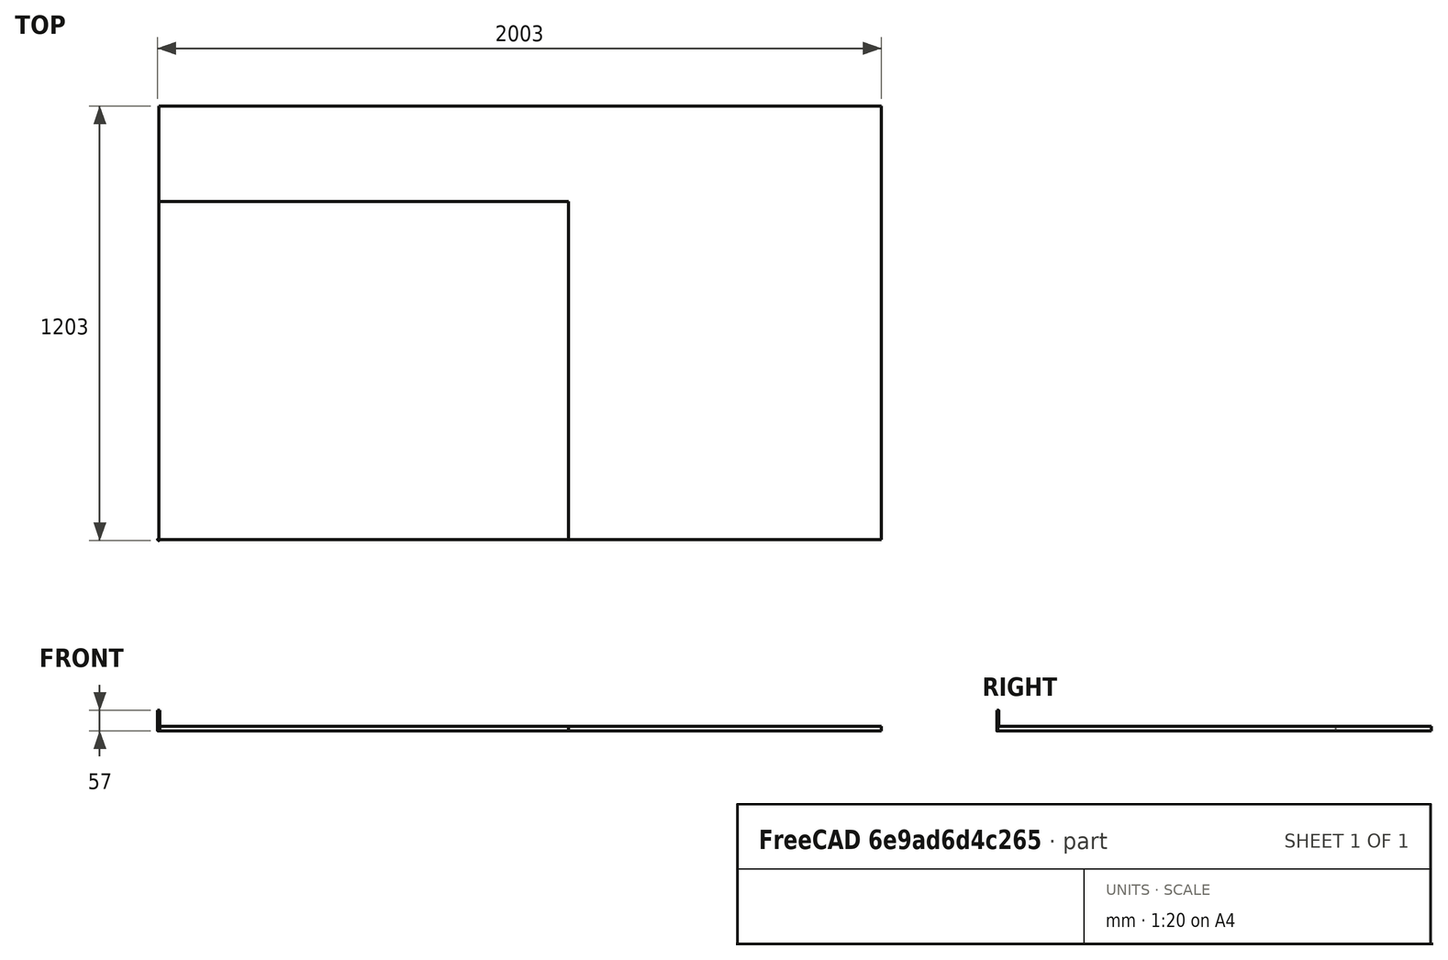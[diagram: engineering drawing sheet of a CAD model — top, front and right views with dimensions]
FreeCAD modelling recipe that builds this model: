
FCSTD DOCUMENT  (FreeCAD 0.21R33771 (Git))
Label: Doll House
License: All rights reserved
LicenseURL: http://en.wikipedia.org/wiki/All_rights_reserved
objects: Part::FeaturePython×10, Sketcher::SketchObject×9, PartDesign::Pad×6, PartDesign::Body×6, Path::FeaturePython×5, PartDesign::Pocket×3, Part::Mirroring×3, App::DocumentObjectGroup×3, App::FeaturePython×1, Mesh::FeaturePython×1
note: 49 computed .brp shape members not serialized (recipe doc carries the construction recipe); baked Part::Feature solids carry a one-line shape summary decoded from their .brp

FEATURE [Sketcher::SketchObject] Sketch
  FullyConstrained = true
  MapMode = 5
  Support = -> [XY_Plane]
  sketch-geometry (4):
    g0: LineSegment StartX=0 StartY=0 StartZ=0 EndX=2000 EndY=0 EndZ=0
    g1: LineSegment StartX=2000 StartY=0 StartZ=0 EndX=2000 EndY=1200 EndZ=0
    g2: LineSegment StartX=2000 StartY=1200 StartZ=0 EndX=0 EndY=1200 EndZ=0
    g3: LineSegment StartX=0 StartY=1200 StartZ=0 EndX=0 EndY=0 EndZ=0
  constraints (11):
    c: Coincident(g0,g1)
    c: Coincident(g1,g2)
    c: Coincident(g2,g3)
    c: Coincident(g3,g0)
    c: Horizontal(g0)
    c: Horizontal(g2)
    c: Vertical(g1)
    c: Vertical(g3)
    c: Coincident(g0,g-1)
    c: DistanceY(g3,g3) = 1200
    c: DistanceX(g0,g0) = 2000
FEATURE [PartDesign::Pad] Pad
  Direction = (0,0,1)
  Length = 12.7
  Length2 = 10
  Profile = -> Sketch
  ReferenceAxis = -> Sketch [N_Axis]
  Type = 0
FEATURE [PartDesign::Body] Body
  Group = -> [Sketch,Pad]
  Origin = -> Origin
  Tip = -> Pad
FEATURE [Sketcher::SketchObject] Sketch001
  FullyConstrained = true
  MapMode = 5
  Support = -> [XY_Plane001]
  sketch-geometry (5):
    g0: LineSegment StartX=0 StartY=0 StartZ=0 EndX=600 EndY=0 EndZ=0
    g1: LineSegment StartX=600 StartY=0 StartZ=0 EndX=600 EndY=350 EndZ=0
    g2: LineSegment StartX=0 StartY=350 StartZ=0 EndX=0 EndY=0 EndZ=0
    g3: LineSegment StartX=0 StartY=350 StartZ=0 EndX=300 EndY=400 EndZ=0
    g4: LineSegment StartX=300 StartY=400 StartZ=0 EndX=600 EndY=350 EndZ=0
  constraints (14):
    c: Coincident(g0,g1)
    c: Coincident(g2,g0)
    c: Horizontal(g0)
    c: Vertical(g1)
    c: Vertical(g2)
    c: Coincident(g0,g-1)
    c: DistanceX(g2,g1) = 600
    c: DistanceY(g1,g1) = 350
    c: Coincident(g3,g4)
    c: Coincident(g4,g1)
    c: Equal(g3,g4)
    c: DistanceY(g0,g3) = 400
    c: Coincident(g2,g3)
    c: DistanceY(g2,g2) = 350
FEATURE [PartDesign::Pad] Pad001
  Direction = (0,0,1)
  Length = 12.7
  Length2 = 10
  Profile = -> Sketch001
  ReferenceAxis = -> Sketch001 [N_Axis]
  Type = 0
FEATURE [PartDesign::Body] Body001  label="Rear"
  Group = -> [Sketch001,Pad001]
  Origin = -> Origin001
  Tip = -> Pad001
FEATURE [Sketcher::SketchObject] Sketch002
  FullyConstrained = false
  MapMode = 5
  Support = -> [XY_Plane002]
  expr: Constraints[10] = 600
  sketch-geometry (4):
    g0: LineSegment StartX=0 StartY=666.245 StartZ=0 EndX=600 EndY=666.245 EndZ=0
    g1: LineSegment StartX=600 StartY=666.245 StartZ=0 EndX=600 EndY=416.245 EndZ=0
    g2: LineSegment StartX=600 StartY=416.245 StartZ=0 EndX=0 EndY=416.245 EndZ=0
    g3: LineSegment StartX=0 StartY=416.245 StartZ=0 EndX=0 EndY=666.245 EndZ=0
  constraints (11):
    c: Coincident(g0,g1)
    c: Coincident(g1,g2)
    c: Coincident(g2,g3)
    c: Coincident(g3,g0)
    c: Horizontal(g0)
    c: Horizontal(g2)
    c: Vertical(g1)
    c: Vertical(g3)
    c: DistanceY(g3,g3) = 250
    c: PointOnObject(g2,g-2)
    c: DistanceX(g0,g0) = 600
FEATURE [PartDesign::Pad] Pad002
  Direction = (0,0,1)
  Length = 12.7
  Length2 = 10
  Profile = -> Sketch002
  ReferenceAxis = -> Sketch002 [N_Axis]
  Type = 0
FEATURE [Sketcher::SketchObject] Sketch004
  FullyConstrained = false
  MapMode = 5
  Support = -> [XY_Plane004]
  sketch-geometry (16):
    g0: LineSegment StartX=624.003 StartY=0 StartZ=0 EndX=874.003 EndY=0 EndZ=0
    g1: LineSegment StartX=874.003 StartY=0 StartZ=0 EndX=874.003 EndY=350 EndZ=0
    g2: LineSegment StartX=874.003 StartY=350 StartZ=0 EndX=624.003 EndY=350 EndZ=0
    g3: LineSegment StartX=624.003 StartY=350 StartZ=0 EndX=624.003 EndY=0 EndZ=0
    g4: LineSegment StartX=659.003 StartY=325 StartZ=0 EndX=731.518 EndY=325 EndZ=0
    g5: LineSegment StartX=731.518 StartY=325 StartZ=0 EndX=731.518 EndY=245.545 EndZ=0
    g6: LineSegment StartX=731.518 StartY=245.545 StartZ=0 EndX=659.003 EndY=245.545 EndZ=0
    g7: LineSegment StartX=659.003 StartY=245.545 StartZ=0 EndX=659.003 EndY=325 EndZ=0
    g8: LineSegment StartX=766.489 StartY=325 StartZ=0 EndX=839.003 EndY=325 EndZ=0
    g9: LineSegment StartX=839.003 StartY=325 StartZ=0 EndX=839.003 EndY=245.545 EndZ=0
    g10: LineSegment StartX=839.003 StartY=245.545 StartZ=0 EndX=766.489 EndY=245.545 EndZ=0
    g11: LineSegment StartX=766.489 StartY=245.545 StartZ=0 EndX=766.489 EndY=325 EndZ=0
    g12: LineSegment StartX=702.358 StartY=126.524 StartZ=0 EndX=796.107 EndY=126.524 EndZ=0
    g13: LineSegment StartX=796.107 StartY=126.524 StartZ=0 EndX=796.107 EndY=45.8183 EndZ=0
    g14: LineSegment StartX=796.107 StartY=45.8183 StartZ=0 EndX=702.358 EndY=45.8183 EndZ=0
    g15: LineSegment StartX=702.358 StartY=45.8183 StartZ=0 EndX=702.358 EndY=126.524 EndZ=0
  constraints (41):
    c: Coincident(g0,g1)
    c: Coincident(g1,g2)
    c: Coincident(g2,g3)
    c: Coincident(g3,g0)
    c: Horizontal(g0)
    c: Horizontal(g2)
    c: Vertical(g1)
    c: Vertical(g3)
    c: DistanceY(g3,g3) = 350
    c: DistanceX(g2,g2) = 250
    c: PointOnObject(g0,g-1)
    c: Coincident(g4,g5)
    c: Coincident(g5,g6)
    c: Coincident(g6,g7)
    c: Coincident(g7,g4)
    c: Horizontal(g4)
    c: Horizontal(g6)
    c: Vertical(g5)
    c: Vertical(g7)
    c: Coincident(g8,g9)
    c: Coincident(g9,g10)
    c: Coincident(g10,g11)
    c: Coincident(g11,g8)
    c: Horizontal(g8)
    c: Horizontal(g10)
    c: Vertical(g9)
    c: Vertical(g11)
    c: Equal(g4,g8)
    c: Equal(g7,g11)
    c: DistanceX(g8,g1) = 35
    c: DistanceX(g2,g4) = 35
    c: DistanceY(g4,g2) = 25
    c: DistanceY(g8,g1) = 25
    c: Coincident(g12,g13)
    c: Coincident(g13,g14)
    c: Coincident(g14,g15)
    c: Coincident(g15,g12)
    c: Horizontal(g12)
    c: Horizontal(g14)
    c: Vertical(g13)
    c: Vertical(g15)
FEATURE [PartDesign::Pad] Pad004
  Direction = (0,0,1)
  Length = 12.7
  Length2 = 10
  Profile = -> Sketch004
  ReferenceAxis = -> Sketch004 [N_Axis]
  Type = 0
FEATURE [Sketcher::SketchObject] Sketch005
  ExternalGeometry = -> [Pad004]
  FullyConstrained = false
  MapMode = 5
  Placement = pos=(0,0,12.7) rot=(0,0,1;0rad)
  Support = -> [Pad004]
  sketch-geometry (10):
    g0: LineSegment StartX=609.961 StartY=176 StartZ=0 EndX=861.003 EndY=176 EndZ=0
    g1: LineSegment StartX=609.961 StartY=163 StartZ=0 EndX=609.961 EndY=176 EndZ=0
    g2: LineSegment StartX=614.691 StartY=0 StartZ=0 EndX=874.003 EndY=0 EndZ=0
    g3: LineSegment StartX=614.691 StartY=13 StartZ=0 EndX=614.691 EndY=0 EndZ=0
    g4: LineSegment StartX=861.003 StartY=350 StartZ=0 EndX=874.003 EndY=350 EndZ=0
    g5: LineSegment StartX=861.003 StartY=13 StartZ=0 EndX=861.003 EndY=163 EndZ=0
    g6: LineSegment StartX=861.003 StartY=163 StartZ=0 EndX=609.961 EndY=163 EndZ=0
    g7: LineSegment StartX=861.003 StartY=13 StartZ=0 EndX=614.691 EndY=13 EndZ=0
    g8: LineSegment StartX=861.003 StartY=176 StartZ=0 EndX=861.003 EndY=350 EndZ=0
    g9: LineSegment StartX=874.003 StartY=350 StartZ=0 EndX=874.003 EndY=0 EndZ=0
  constraints (26):
    c: Coincident(g6,g1)
    c: Coincident(g1,g0)
    c: Horizontal(g0)
    c: Vertical(g1)
    c: Coincident(g7,g3)
    c: Coincident(g3,g2)
    c: Horizontal(g2)
    c: Vertical(g3)
    c: Coincident(g8,g4)
    c: Horizontal(g4)
    c: Vertical(g5)
    c: DistanceX(g4,g4) = 13
    c: Coincident(g5,g7)
    c: Coincident(g5,g6)
    c: Coincident(g8,g0)
    c: Coincident(g2,g9)
    c: DistanceY(g2,g5) = 13
    c: DistanceX(g5,g2) = 13
    c: Coincident(g4,g9)
    c: Coincident(g4,g-3)
    c: DistanceX(g0,g4) = 13
    c: DistanceY(g3,g3) = 13
    c: DistanceY(g1,g1) = 13
    c: Coincident(g2,g-3)
    c: DistanceY(g5,g5) = 150
    c: Parallel(g-1,g6)
FEATURE [PartDesign::Pocket] Pocket
  BaseFeature = -> Pad004
  Direction = (0,0,-1)
  Length = 5
  Length2 = 5
  Profile = -> Sketch005
  ReferenceAxis = -> Sketch005 [N_Axis]
  Type = 0
FEATURE [PartDesign::Body] Body004  label="LSide"
  Group = -> [Sketch004,Pad004,Sketch005,Pocket]
  Origin = -> Origin004
  Tip = -> Pocket
FEATURE [Part::Mirroring] Mirror  label="LSide (mirrored)"
  Base = (879.242,357.189,0)
  Normal = (-1,0,0)
  Source = -> Body004
FEATURE [Sketcher::SketchObject] Sketch006
  FullyConstrained = false
  MapMode = 5
  Support = -> [XY_Plane005]
  sketch-geometry (4):
    g0: LineSegment StartX=617.937 StartY=364.155 StartZ=0 EndX=867.937 EndY=364.155 EndZ=0
    g1: LineSegment StartX=867.937 StartY=364.155 StartZ=0 EndX=867.937 EndY=689.155 EndZ=0
    g2: LineSegment StartX=867.937 StartY=689.155 StartZ=0 EndX=617.937 EndY=689.155 EndZ=0
    g3: LineSegment StartX=617.937 StartY=689.155 StartZ=0 EndX=617.937 EndY=364.155 EndZ=0
  constraints (10):
    c: Coincident(g0,g1)
    c: Coincident(g1,g2)
    c: Coincident(g2,g3)
    c: Coincident(g3,g0)
    c: Horizontal(g0)
    c: Horizontal(g2)
    c: Vertical(g1)
    c: Vertical(g3)
    c: DistanceY(g3,g3) = 325
    c: DistanceX(g2,g2) = 250
FEATURE [PartDesign::Pad] Pad005
  Direction = (0,0,1)
  Length = 12.7
  Length2 = 10
  Profile = -> Sketch006
  ReferenceAxis = -> Sketch006 [N_Axis]
  Type = 0
FEATURE [Sketcher::SketchObject] Sketch007
  ExternalGeometry = -> [Pad005]
  FullyConstrained = false
  MapMode = 5
  Placement = pos=(0,0,12.7) rot=(0,0,1;0rad)
  Support = -> [Pad005]
  sketch-geometry (6):
    g0: LineSegment StartX=854.937 StartY=702.88 StartZ=0 EndX=854.937 EndY=385.155 EndZ=0
    g1: LineSegment StartX=854.937 StartY=385.155 StartZ=0 EndX=607.793 EndY=385.155 EndZ=0
    g2: LineSegment StartX=607.793 StartY=385.155 StartZ=0 EndX=607.793 EndY=370.155 EndZ=0
    g3: LineSegment StartX=607.793 StartY=370.155 StartZ=0 EndX=885.781 EndY=370.155 EndZ=0
    g4: LineSegment StartX=885.781 StartY=370.155 StartZ=0 EndX=885.781 EndY=702.88 EndZ=0
    g5: LineSegment StartX=885.781 StartY=702.88 StartZ=0 EndX=854.937 EndY=702.88 EndZ=0
  constraints (15):
    c: Vertical(g0)
    c: Coincident(g0,g1)
    c: Horizontal(g1)
    c: Coincident(g1,g2)
    c: Vertical(g2)
    c: Coincident(g2,g3)
    c: Horizontal(g3)
    c: Coincident(g3,g4)
    c: Vertical(g4)
    c: Coincident(g4,g5)
    c: Coincident(g5,g0)
    c: Horizontal(g5)
    c: DistanceY(g2,g2) = 15
    c: DistanceY(g1,g-3) = 304
    c: DistanceX(g0,g-3) = 13
FEATURE [PartDesign::Pocket] Pocket001
  BaseFeature = -> Pad005
  Direction = (0,0,-1)
  Length = 5
  Length2 = 5
  Profile = -> Sketch007
  ReferenceAxis = -> Sketch007 [N_Axis]
  Type = 0
FEATURE [PartDesign::Body] Body005  label="Roof"
  Group = -> [Sketch006,Pad005,Sketch007,Pocket001]
  Origin = -> Origin005
  Tip = -> Pocket001
FEATURE [Part::Mirroring] Mirror001  label="Roof (mirrored)"
  Base = (875.299,692.275,0)
  Normal = (-1,0,0)
  Source = -> Body005
FEATURE [Sketcher::SketchObject] Sketch008
  ExternalGeometry = -> [Pad002]
  FullyConstrained = false
  MapMode = 5
  Placement = pos=(0,0,12.7) rot=(0,0,1;0rad)
  Support = -> [Pad002]
  expr: Constraints[9] = (600 - 13) / 2
  sketch-geometry (4):
    g0: LineSegment StartX=293.5 StartY=675.977 StartZ=0 EndX=306.5 EndY=675.977 EndZ=0
    g1: LineSegment StartX=306.5 StartY=675.977 StartZ=0 EndX=306.5 EndY=411.033 EndZ=0
    g2: LineSegment StartX=306.5 StartY=411.033 StartZ=0 EndX=293.5 EndY=411.033 EndZ=0
    g3: LineSegment StartX=293.5 StartY=411.033 StartZ=0 EndX=293.5 EndY=675.977 EndZ=0
  constraints (10):
    c: Coincident(g0,g1)
    c: Coincident(g1,g2)
    c: Coincident(g2,g3)
    c: Coincident(g3,g0)
    c: Horizontal(g0)
    c: Horizontal(g2)
    c: Vertical(g1)
    c: Vertical(g3)
    c: DistanceX(g0,g0) = 13
    c: DistanceX(g-3,g2) = 293.5
FEATURE [PartDesign::Pocket] Pocket002
  BaseFeature = -> Pad002
  Direction = (0,0,-1)
  Length = 5
  Length2 = 5
  Profile = -> Sketch008
  ReferenceAxis = -> Sketch008 [N_Axis]
  Type = 0
FEATURE [PartDesign::Body] Body002  label="Bottom"
  Group = -> [Sketch002,Pad002,Sketch008,Pocket002]
  Origin = -> Origin002
  Tip = -> Pocket002
FEATURE [Part::Mirroring] Mirror002  label="Bottom (mirrored)"
  Base = (-4.23029,675.935,0)
  Normal = (0,-1,0)
  Source = -> Body002
FEATURE [Sketcher::SketchObject] Sketch009
  FullyConstrained = false
  MapMode = 5
  Support = -> [XY_Plane006]
  sketch-geometry (8):
    g0: LineSegment StartX=620.131 StartY=875.169 StartZ=0 EndX=855.131 EndY=875.169 EndZ=0
    g1: LineSegment StartX=855.131 StartY=875.169 StartZ=0 EndX=855.131 EndY=716.169 EndZ=0
    g2: LineSegment StartX=855.131 StartY=716.169 StartZ=0 EndX=620.131 EndY=716.169 EndZ=0
    g3: LineSegment StartX=620.131 StartY=716.169 StartZ=0 EndX=620.131 EndY=875.169 EndZ=0
    g4: LineSegment StartX=693.547 StartY=834.52 StartZ=0 EndX=756.678 EndY=834.52 EndZ=0
    g5: LineSegment StartX=756.678 StartY=834.52 StartZ=0 EndX=756.678 EndY=726.826 EndZ=0
    g6: LineSegment StartX=756.678 StartY=726.826 StartZ=0 EndX=693.547 EndY=726.826 EndZ=0
    g7: LineSegment StartX=693.547 StartY=726.826 StartZ=0 EndX=693.547 EndY=834.52 EndZ=0
  constraints (18):
    c: Coincident(g0,g1)
    c: Coincident(g1,g2)
    c: Coincident(g2,g3)
    c: Coincident(g3,g0)
    c: Horizontal(g0)
    c: Horizontal(g2)
    c: Vertical(g1)
    c: Vertical(g3)
    c: DistanceX(g0,g0) = 235
    c: DistanceY(g3,g3) = 159
    c: Coincident(g4,g5)
    c: Coincident(g5,g6)
    c: Coincident(g6,g7)
    c: Coincident(g7,g4)
    c: Horizontal(g4)
    c: Horizontal(g6)
    c: Vertical(g5)
    c: Vertical(g7)
FEATURE [PartDesign::Pad] Pad006
  Direction = (0,0,1)
  Length = 12.7
  Length2 = 10
  Profile = -> Sketch009
  ReferenceAxis = -> Sketch009 [N_Axis]
  Type = 0
FEATURE [PartDesign::Body] Body006  label="Partition"
  Group = -> [Sketch009,Pad006]
  Origin = -> Origin006
  Tip = -> Pad006
FEATURE [App::FeaturePython] SetupSheet  # Path/CAM operation (typed FeaturePython)
  ClearanceHeightExpression = OpStockZMax+SetupSheet.ClearanceHeightOffset
  ClearanceHeightOffset = 5
  CoolantMode = 0
  CoolantModes = None | Flood | Mist
  FinalDepthExpression = OpFinalDepth
  HorizRapid = 0
  SafeHeightExpression = OpStockZMax+SetupSheet.SafeHeightOffset
  SafeHeightOffset = 3
  StartDepthExpression = OpStartDepth
  StepDownExpression = OpToolDiameter
  VertRapid = 0
FEATURE [Part::FeaturePython] Clone  label="Model-Bottom"  # Draft clone (typed FeaturePython)
  AttacherType = Attacher::AttachEngine3D
  Fuse = false
  Objects = -> [Body002]
  PathResource = Model
  Scale = (1,1,1)
FEATURE [Part::FeaturePython] Clone001  label="Model-Bottom (mirrored)"  # Draft clone (typed FeaturePython)
  AttacherType = Attacher::AttachEngine3D
  Fuse = false
  Objects = -> [Mirror002]
  PathResource = Model
  Scale = (1,1,1)
FEATURE [Part::FeaturePython] Clone002  label="Model-LSide"  # Draft clone (typed FeaturePython)
  AttacherType = Attacher::AttachEngine3D
  Fuse = false
  Objects = -> [Body004]
  PathResource = Model
  Scale = (1,1,1)
FEATURE [Part::FeaturePython] Clone003  label="Model-LSide (mirrored)"  # Draft clone (typed FeaturePython)
  AttacherType = Attacher::AttachEngine3D
  Fuse = false
  Objects = -> [Mirror]
  PathResource = Model
  Scale = (1,1,1)
FEATURE [Part::FeaturePython] Clone004  label="Model-Partition"  # Draft clone (typed FeaturePython)
  AttacherType = Attacher::AttachEngine3D
  Fuse = false
  Objects = -> [Body006]
  PathResource = Model
  Scale = (1,1,1)
FEATURE [Part::FeaturePython] Clone005  label="Model-Rear"  # Draft clone (typed FeaturePython)
  AttacherType = Attacher::AttachEngine3D
  Fuse = false
  Objects = -> [Body001]
  PathResource = Model
  Scale = (1,1,1)
FEATURE [Part::FeaturePython] Clone006  label="Model-Roof"  # Draft clone (typed FeaturePython)
  AttacherType = Attacher::AttachEngine3D
  Fuse = false
  Objects = -> [Body005]
  PathResource = Model
  Scale = (1,1,1)
FEATURE [Part::FeaturePython] Clone007  label="Model-Roof (mirrored)"  # Draft clone (typed FeaturePython)
  AttacherType = Attacher::AttachEngine3D
  Fuse = false
  Objects = -> [Mirror001]
  PathResource = Model
  Scale = (1,1,1)
FEATURE [App::DocumentObjectGroup] Model
  Group = -> [Clone,Clone001,Clone002,Clone003,Clone004,Clone005,Clone006,Clone007]
FEATURE [Part::FeaturePython] ToolBit001  label="6mm Endmill"  # Path/CAM toolbit (typed FeaturePython)
  BitPropertyNames = Chipload | CuttingEdgeHeight | Diameter | Flutes | Length | Material | ShankDiameter | SpindleDirection
  BitShape = /app/freecad/Mod/Path/Tools/Shape/endmill.fcstd
  Chipload = 0
  CuttingEdgeHeight = 13
  Diameter = 6
  File = <userpath>/Documents/Sherline/FreeCAD/Bit/6mm_Endmill.fctb
  Flutes = 2
  Length = 57
  Material = 0
  ShankDiameter = 6
  ShapeName = endmill
  SpindleDirection = 0
FEATURE [Path::FeaturePython] _mm_Endmill  label="6mm Endmill001"  # Path/CAM operation (typed FeaturePython)
  HorizFeed = 20
  HorizRapid = 0
  SpindleDir = 0
  SpindleSpeed = 12000
  Tool = -> ToolBit001
  ToolNumber = 2
  VertFeed = 5
  VertRapid = 0
  expr: HorizRapid = SetupSheet.HorizRapid
  expr: VertRapid = SetupSheet.VertRapid
FEATURE [App::DocumentObjectGroup] Tools
  Group = -> [_mm_Endmill]
FEATURE [Path::FeaturePython] Profile  # Path/CAM operation (typed FeaturePython)
  Active = true
  AreaParams:
    Tolerance = 1e-07
    FitArcs = True
    Simplify = False
    CleanDistance = 0.0
    Accuracy = 0.01
    Unit = 1.0
    MinArcPoints = 4
    MaxArcPoints = 100
    ClipperScale = 10000000.0
    Fill = 0
    Coplanar = 0
    Reorient = True
    Outline = False
    Explode = False
    OpenMode = 0
    Deflection = 0.01
    SubjectFill = 0
    ClipFill = 0
    Offset = 3.0
    ExtraPass = 0
    Stepover = 0.0
    LastStepover = 0.0
    JoinType = 0
    EndType = 0
    MiterLimit = 2.0
    RoundPrecision = 0.0
    PocketMode = 0
    ToolRadius = 1.0
    PocketExtraOffset = 0.0
    PocketStepover = 0.0
    PocketLastStepover = 0.0
    FromCenter = False
    Angle = 45.0
    AngleShift = 0.0
    Shift = 0.0
    Thicken = False
    SectionCount = -1
    Stepdown = 1.0
    SectionOffset = 0.0
    SectionTolerance = 1e-07
    SectionMode = 2
    Project = False
  Base = -> [Clone005,Clone002,Clone003,Clone,Clone001,Clone004,Clone006,Clone007]
  ClearanceHeight = 17.7
  CoolantMode = 0
  CycleTime = 00:38:41
  Direction = 0
  FinalDepth = 0
  HandleMultipleFeatures = 0
  JoinType = 0
  MiterLimit = 0.1
  OffsetExtra = 0
  OpFinalDepth = 0
  OpStartDepth = 12.7
  OpStockZMax = 12.7
  OpStockZMin = 0
  OpToolDiameter = 6
  PathParams = {'orientation': 1, 'feedrate': 20.0, 'feedrate_v': 5.0, 'verbose': True, 'resume_height': 15.7, 'retraction': 17.7, 'return_end': True, 'preamble': False, 'start': Vector (884.4370746882124, 352.9996973103541, 17.7)}
  Placement = pos=(0,0,0) rot=(0,0,1;-1.5708rad)
  SafeHeight = 15.7
  Side = 0
  SplitArcs = false
  StartDepth = 12.7
  StartPoint = (0,0,0)
  StepDown = 4
  ToolController = -> _mm_Endmill
  UseComp = true
  UseStartPoint = false
  processCircles = false
  processHoles = false
  processPerimeter = true
  expr: ClearanceHeight = OpStockZMax + SetupSheet.ClearanceHeightOffset
  expr: FinalDepth = 0
  expr: SafeHeight = OpStockZMax + SetupSheet.SafeHeightOffset
  expr: StartDepth = 12.7
  expr: StepDown = 4
FEATURE [Part::FeaturePython] Stock  # WARN: FeaturePython — macro-defined, semantics opaque (R4)
  Height = 12.7
  Length = 1134.48
  StockType = CreateBox
  Width = 935.63
FEATURE [Path::FeaturePython] Profile001  # Path/CAM operation (typed FeaturePython)
  Active = true
  AreaParams:
    Tolerance = 1e-07
    FitArcs = True
    Simplify = False
    CleanDistance = 0.0
    Accuracy = 0.01
    Unit = 1.0
    MinArcPoints = 4
    MaxArcPoints = 100
    ClipperScale = 10000000.0
    Fill = 0
    Coplanar = 0
    Reorient = True
    Outline = False
    Explode = False
    OpenMode = 0
    Deflection = 0.01
    SubjectFill = 0
    ClipFill = 0
    Offset = -3.0
    ExtraPass = 0
    Stepover = 0.0
    LastStepover = 0.0
    JoinType = 0
    EndType = 0
    MiterLimit = 2.0
    RoundPrecision = 0.0
    PocketMode = 0
    ToolRadius = 1.0
    PocketExtraOffset = 0.0
    PocketStepover = 0.0
    PocketLastStepover = 0.0
    FromCenter = False
    Angle = 45.0
    AngleShift = 0.0
    Shift = 0.0
    Thicken = False
    SectionCount = -1
    Stepdown = 1.0
    SectionOffset = 0.0
    SectionTolerance = 1e-07
    SectionMode = 2
    Project = False
  Base = -> [Clone004,Clone002,Clone003]
  ClearanceHeight = 17.7
  CoolantMode = 0
  CycleTime = 00:09:37
  Direction = 0
  FinalDepth = 0
  HandleMultipleFeatures = 0
  JoinType = 0
  MiterLimit = 0.1
  OffsetExtra = 0
  OpFinalDepth = 12.7
  OpStartDepth = 16.7
  OpStockZMax = 12.7
  OpStockZMin = 0
  OpToolDiameter = 6
  PathParams = {'orientation': 1, 'feedrate': 20.0, 'feedrate_v': 5.0, 'verbose': True, 'resume_height': 15.7, 'retraction': 17.7, 'return_end': True, 'preamble': False, 'start': Vector (793.1072998999998, 123.5243609, 17.7)}
  Placement = pos=(0,0,0) rot=(0,0,1;-1.5708rad)
  SafeHeight = 15.7
  Side = 1
  SplitArcs = false
  StartDepth = 12.7
  StartPoint = (0,0,0)
  StepDown = 4
  ToolController = -> _mm_Endmill
  UseComp = true
  UseStartPoint = false
  processCircles = false
  processHoles = false
  processPerimeter = true
  expr: ClearanceHeight = OpStockZMax + SetupSheet.ClearanceHeightOffset
  expr: FinalDepth = 0
  expr: SafeHeight = OpStockZMax + SetupSheet.SafeHeightOffset
  expr: StartDepth = 12.7
  expr: StepDown = 4
FEATURE [Path::FeaturePython] Pocket_Shape  # Path/CAM operation (typed FeaturePython)
  Active = true
  AreaParams:
    Tolerance = 1e-07
    FitArcs = True
    Simplify = False
    CleanDistance = 0.0
    Accuracy = 0.01
    Unit = 1.0
    MinArcPoints = 4
    MaxArcPoints = 100
    ClipperScale = 10000000.0
    Fill = 0
    Coplanar = 0
    Reorient = True
    Outline = False
    Explode = False
    OpenMode = 0
    Deflection = 0.01
    SubjectFill = 0
    ClipFill = 0
    Offset = 0.0
    ExtraPass = 0
    Stepover = 0.0
    LastStepover = 0.0
    JoinType = 0
    EndType = 0
    MiterLimit = 2.0
    RoundPrecision = 0.0
    PocketMode = 2
    ToolRadius = 3.0
    PocketExtraOffset = 0.0
    PocketStepover = 6.0
    PocketLastStepover = 0.0
    FromCenter = True
    Angle = 90.0
    AngleShift = 0.0
    Shift = 0.0
    Thicken = False
    SectionCount = -1
    Stepdown = 1.0
    SectionOffset = 0.0
    SectionTolerance = 1e-07
    SectionMode = 2
    Project = False
  Base = -> [Clone001,Clone,Clone006,Clone007,Clone002,Clone003]
  ClearanceHeight = 17.7
  CoolantMode = 0
  CutMode = 0
  CycleTime = 00:36:53
  ExtensionCorners = true
  ExtensionLengthDefault = 3
  ExtraOffset = 0
  FinalDepth = 7.7
  FinishDepth = 0
  KeepToolDown = false
  MinTravel = false
  OffsetPattern = 1
  OpFinalDepth = 7.7
  OpStartDepth = 12.7
  OpStockZMax = 12.7
  OpStockZMin = 0
  OpToolDiameter = 6
  PathParams = {'orientation': 1, 'feedrate': 20.0, 'feedrate_v': 5.0, 'verbose': True, 'resume_height': 15.7, 'retraction': 17.7, 'return_end': True, 'preamble': False, 'start': Vector (891.9796896252973, 168.0881129, 17.7)}
  Placement = pos=(0,0,0) rot=(0,0,1;-1.5708rad)
  PocketLastStepOver = 0
  SafeHeight = 15.7
  SplitArcs = false
  StartAt = 0
  StartDepth = 12.7
  StartPoint = (0,0,0)
  StepDown = 4
  StepOver = 100
  ToolController = -> _mm_Endmill
  UseOutline = true
  UseStartPoint = false
  ZigZagAngle = 90
  expr: ClearanceHeight = OpStockZMax + SetupSheet.ClearanceHeightOffset
  expr: ExtensionLengthDefault = OpToolDiameter / 2
  expr: FinalDepth = OpFinalDepth
  expr: SafeHeight = OpStockZMax + SetupSheet.SafeHeightOffset
  expr: StartDepth = 12.7
  expr: StepDown = 4
FEATURE [App::DocumentObjectGroup] Operations
  Group = -> [Profile001,Pocket_Shape,Profile]
FEATURE [Path::FeaturePython] Job  # Path/CAM operation (typed FeaturePython)
  CycleTime = 01:25:11
  Fixtures = G54
  GeometryTolerance = 0.01
  JobType = 0
  Model = -> Model
  Operations = -> Operations
  OrderOutputBy = 0
  PostProcessor = 4
  PostProcessorOutputFile = %D/%d-%j.ngc
  SetupSheet = -> SetupSheet
  SplitOutput = false
  Stock = -> Stock
  Tools = -> Tools
FEATURE [Mesh::FeaturePython] CutMaterial  # WARN: FeaturePython — macro-defined, semantics opaque (R4)
